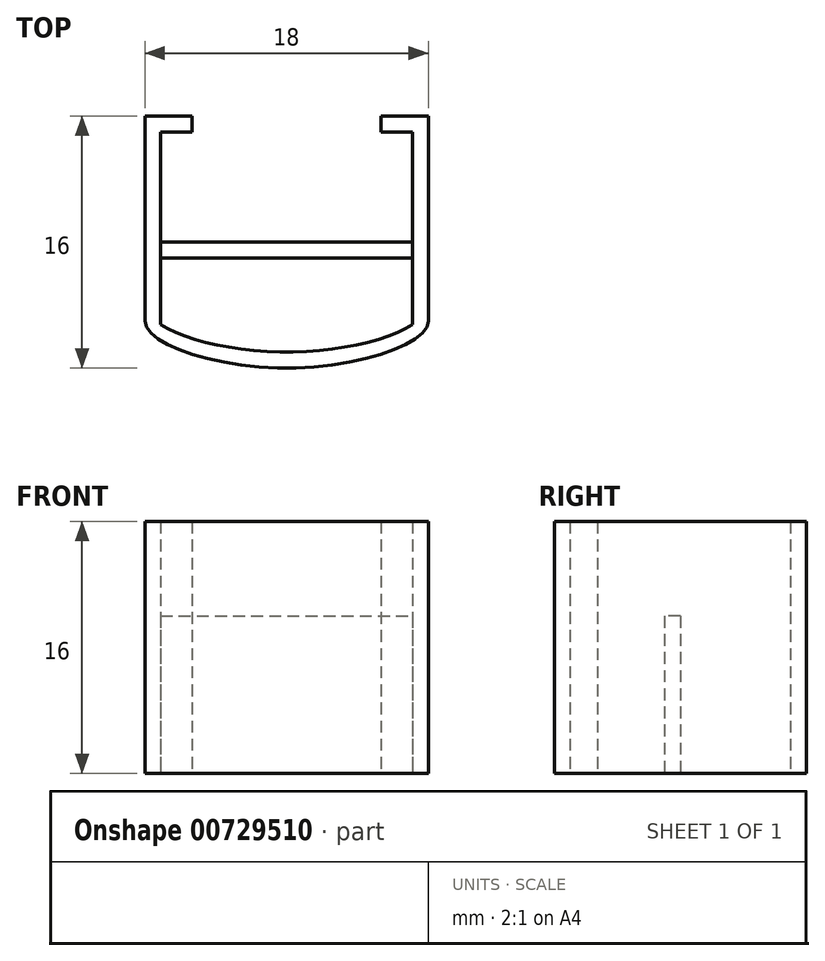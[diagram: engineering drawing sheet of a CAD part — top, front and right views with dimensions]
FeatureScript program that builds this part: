
annotation { "Feature Type Name" : "Feature", "Feature Type Description" : "" }
export const myFeature = defineFeature(function(context is Context, id is Id, definition is map)
    precondition{}
    {
        {
            var Q0;
            Q0=qCreatedBy(makeId("Top.planeOp"),FACE);
            var sketch = newSketch(context, id + "F0", { "sketchPlane" : qUnion([Q0])});
            skLineSegment(sketch, "E0", {"start": v(0, 0) * mm, "end": v(-9, 0) * mm, "construction": true});
            skLineSegment(sketch, "E1", {"start": v(0, 0) * mm, "end": v(9, 0) * mm, "construction": true});
            skLineSegment(sketch, "E2", {"start": v(0, 0) * mm, "end": v(0, 9) * mm, "construction": true});
            skLineSegment(sketch, "E3", {"start": v(0, 0) * mm, "end": v(0, -7) * mm, "construction": true});
            skLineSegment(sketch, "E4", {"start": v(-9, 0) * mm, "end": v(-9, 9) * mm});
            skLineSegment(sketch, "E5", {"start": v(9, 0) * mm, "end": v(9, 9) * mm});
            skLineSegment(sketch, "E6", {"start": v(-9, 9) * mm, "end": v(-6, 9) * mm});
            skLineSegment(sketch, "E7", {"start": v(9, 9) * mm, "end": v(6, 9) * mm});
            skLineSegment(sketch, "E8", {"start": v(-9, 0) * mm, "end": v(-9, -4) * mm});
            skLineSegment(sketch, "E9", {"start": v(9, 0) * mm, "end": v(9, -4) * mm});
            skLineSegment(sketch, "E10", {"start": v(0, 0) * mm, "end": v(0, -1) * mm, "construction": true});
            skFitSpline(sketch, "E11", {"points": [v(-9, -4) * mm, v(0, -7) * mm, v(9, -4) * mm, v(0, -1) * mm, v(-9, -4) * mm]});
            skLineSegment(sketch, "E12", {"start": v(0, 0) * mm, "end": v(0, 0) * mm});
            skLineSegment(sketch, "E13", {"start": v(0, 0) * mm, "end": v(0, -6) * mm, "construction": true});
            skLineSegment(sketch, "E14", {"start": v(-9, 0) * mm, "end": v(-9, -3) * mm, "construction": true});
            skLineSegment(sketch, "E15", {"start": v(9, 0) * mm, "end": v(9, -3) * mm, "construction": true});
            skFitSpline(sketch, "E16", {"points": [v(-9, -3) * mm, v(0, 0) * mm, v(9, -3) * mm, v(0, -6) * mm, v(-9, -3) * mm]});
            skLineSegment(sketch, "E17", {"start": v(-6, 9) * mm, "end": v(-6, 8) * mm});
            skLineSegment(sketch, "E18", {"start": v(6, 9) * mm, "end": v(6, 8) * mm});
            skLineSegment(sketch, "E19", {"start": v(6, 8) * mm, "end": v(8, 8) * mm});
            skLineSegment(sketch, "E20", {"start": v(-6, 8) * mm, "end": v(-8, 8) * mm});
            skLineSegment(sketch, "E21", {"start": v(-8, 8) * mm, "end": v(-8, -4.25) * mm});
            skLineSegment(sketch, "E22", {"start": v(8, 8) * mm, "end": v(8, -4.25) * mm});
            skPoint(sketch, "E23", {"position": v(-8, 0) * mm});
            skLineSegment(sketch, "E24.bottom", {"start": v(-8, 0) * mm, "end": v(8, 0) * mm});
            skLineSegment(sketch, "E24.top", {"start": v(-8, 1) * mm, "end": v(8, 1) * mm});
            skLineSegment(sketch, "E24.left", {"start": v(-8, 0) * mm, "end": v(-8, 1) * mm});
            skLineSegment(sketch, "E24.right", {"start": v(8, 0) * mm, "end": v(8, 1) * mm});
            skSolve(sketch);
        }
        {
            var Q0;
            {var subQ6=sQuery(id+"F0.wireOp",EDGE,"E4");Q0=makeQuery(id+"F0.imprint","IMPRINT",FACE,{"disambiguationData":[TD([[makeQuery(id+"F0.imprint","IMPRINT",EDGE,{"derivedFrom":subQ6}),-1.0]])]});}
            var Q1;
            {var subQ0=sQuery(id+"F0.wireOp",EDGE,"E21");var subQ1=sQuery(id+"F0.wireOp",EDGE,"E11");var subQ2=makeQuery(id+"F0.imprint","INTERSECT",VERTEX,{"derivedFrom":[subQ1,subQ0]});Q1=makeQuery(id+"F0.imprint","IMPRINT",FACE,{"disambiguationData":[TD([[makeQuery(id+"F0.imprint","IMPRINT",EDGE,{"disambiguationData":[TD([[subQ2,-1.0]])],"derivedFrom":subQ1}),-1.0]])]});}
            var Q2;
            {var subQ0=sQuery(id+"F0.wireOp",EDGE,"E11");var subQ1=sQuery(id+"F0.wireOp",EDGE,"E8");var subQ2=makeQuery(id+"F0.imprint","INTERSECT",VERTEX,{"derivedFrom":[subQ1,subQ0]});Q2=makeQuery(id+"F0.imprint","IMPRINT",FACE,{"disambiguationData":[TD([[makeQuery(id+"F0.imprint","IMPRINT",EDGE,{"disambiguationData":[TD([[subQ2,1.0]])],"derivedFrom":subQ1}),1.0]])]});}
            var Q3;
            {var subQ0=sQuery(id+"F0.wireOp",EDGE,"E21");var subQ1=sQuery(id+"F0.wireOp",EDGE,"E11");var subQ2=makeQuery(id+"F0.imprint","INTERSECT",VERTEX,{"derivedFrom":[subQ1,subQ0]});Q3=makeQuery(id+"F0.imprint","IMPRINT",FACE,{"disambiguationData":[TD([[makeQuery(id+"F0.imprint","IMPRINT",EDGE,{"disambiguationData":[TD([[subQ2,-1.0]])],"derivedFrom":subQ1}),1.0]])]});}
            var Q4;
            {var subQ0=sQuery(id+"F0.wireOp",EDGE,"E11");var subQ7=makeQuery(id+"F0.imprint","INTERSECT",VERTEX,{"derivedFrom":[sQuery(id+"F0.wireOp",EDGE,"E8"),subQ0]});Q4=makeQuery(id+"F0.imprint","IMPRINT",FACE,{"disambiguationData":[TD([[makeQuery(id+"F0.imprint","IMPRINT",EDGE,{"disambiguationData":[TD([[subQ7,-1.0]])],"derivedFrom":subQ0}),1.0]])]});}
            var Q5;
            {var subQ0=sQuery(id+"F0.wireOp",EDGE,"E16");var subQ1=sQuery(id+"F0.wireOp",EDGE,"E11");var subQ2=makeQuery(id+"F0.imprint","INTERSECT",VERTEX,{"disambiguationData":[OD(0.0)],"derivedFrom":[subQ1,subQ0]});Q5=makeQuery(id+"F0.imprint","IMPRINT",FACE,{"disambiguationData":[TD([[makeQuery(id+"F0.imprint","IMPRINT",EDGE,{"disambiguationData":[TD([[subQ2,-1.0]])],"derivedFrom":subQ1}),1.0]])]});}
            var Q6;
            {var subQ0=sQuery(id+"F0.wireOp",EDGE,"E16");var subQ1=sQuery(id+"F0.wireOp",EDGE,"E11");var subQ2=makeQuery(id+"F0.imprint","INTERSECT",VERTEX,{"disambiguationData":[OD(0.0)],"derivedFrom":[subQ1,subQ0]});Q6=makeQuery(id+"F0.imprint","IMPRINT",FACE,{"disambiguationData":[TD([[makeQuery(id+"F0.imprint","IMPRINT",EDGE,{"disambiguationData":[TD([[subQ2,-1.0]])],"derivedFrom":subQ1}),-1.0]])]});}
            var Q7;
            {var subQ5=sQuery(id+"F0.wireOp",EDGE,"E5");Q7=makeQuery(id+"F0.imprint","IMPRINT",FACE,{"disambiguationData":[TD([[makeQuery(id+"F0.imprint","IMPRINT",EDGE,{"derivedFrom":subQ5}),1.0]])]});}
            var Q8;
            {var subQ0=sQuery(id+"F0.wireOp",EDGE,"E11");var subQ1=sQuery(id+"F0.wireOp",EDGE,"E9");var subQ2=makeQuery(id+"F0.imprint","INTERSECT",VERTEX,{"derivedFrom":[subQ1,subQ0]});Q8=makeQuery(id+"F0.imprint","IMPRINT",FACE,{"disambiguationData":[TD([[makeQuery(id+"F0.imprint","IMPRINT",EDGE,{"disambiguationData":[TD([[subQ2,1.0]])],"derivedFrom":subQ1}),-1.0]])]});}
            extrude(context, id + "F1", {"entities" : qUnion([Q0, Q1, Q2, Q3, Q4, Q5, Q6, Q7, Q8]), "depth" : 16 * mm, "offsetDistance" : 25 * mm});
        }
        {
            var Q0;
            Q0=makeQuery(id+"F0.imprint","IMPRINT",FACE,{"disambiguationData":[TD([[makeQuery(id+"F0.imprint","IMPRINT",EDGE,{"derivedFrom":sQuery(id+"F0.wireOp",EDGE,"E24.top")}),-1.0]])]});
            extrude(context, id + "F2", {"entities" : qUnion([Q0]), "operationType" : NewBodyOperationType.ADD, "depth" : 10 * mm, "offsetDistance" : 25 * mm});
        }
    });
